# Revit family: Bath-Freestanding-KOHLER-Veil-K-8331
name_source: partatom
category: Plumbing Fixtures
revit_build: Autodesk Revit 2015 (Build: 20140606_1530(x64)
units: mm (PartAtom-declared; Revit-internal decimal feet)

## types (1)
- K-8331-0-White
    ADA Compliant = Yes
    Assembly Code = D2010500
    Date Modified = 09/08/2017
    Default Elevation = 0"
    Description = Veil 66inch x 36inch freestanding bath with center toe-tap drain
    Finish = Kohler-Lithocast-0-White
    Flow Rate = 0 GPM
    Height = 24 9/16"
    Inlet Connector = Inlet Connection
    Length = 66"
    Manufacturer = Kohler
    MasterFormat 1995 = 15410
    MasterFormat 2004 = 22.41.19
    Material = KOHLER Lithocast
    Model = K-8331-0
    Outlet Connector = Outlet Connection
    Pressure = 0.00 psi
    Product Documentation Link = http://www.us.kohler.com
    Product Name = Veil
    Product Page URL = http://www.us.kohler.com
    Type = 0
    URL = http://www.us.kohler.com
    Waste Connection = Yes
    Width = 36 7/8"

## geometry (parser evidence)
native form markers: Sweep x5
no freeform markers — native parametric forms only
